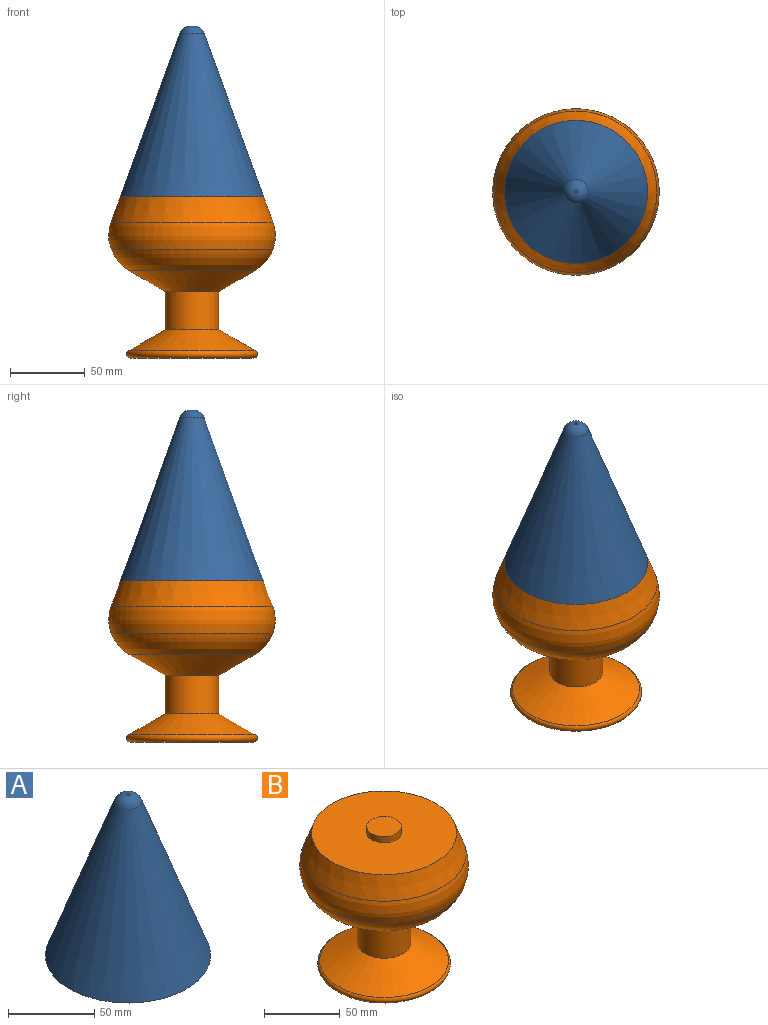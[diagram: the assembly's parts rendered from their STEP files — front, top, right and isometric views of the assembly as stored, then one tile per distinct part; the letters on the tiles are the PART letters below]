
ASSEMBLY  parts=2 mates=1
PART A: 6 faces, bbox 95.9x95.9x114.3 mm
  f0: plane 1.99x1.99mm, normal (0,0,1), area 3.1mm2, adj f1
  f1: torus R=0.99mm, axis (0,0,1), area 298.2mm2, adj f0,f2
  f2: cone r=61.8mm half-angle=20deg, axis (0,0,-1), area 20491.8mm2, adj f1,f3
  f3: plane 95.86x95.86mm, normal (0,0,-1), area 6710.8mm2, adj f2,f4
  f4: cylinder r=12.7mm len=25.4mm, axis (0,0,-1), area 506.7mm2, adj f3,f5
  f5: plane 25.4x25.4mm, normal (0,0,-1), area 506.7mm2, adj f4
PART B: 12 faces, bbox 120.7x120.7x113 mm
  f0: cone r=61.8mm half-angle=20deg, axis (0,0,-1), area 5816mm2, adj f7,f8
  f1: cone r=50.8mm half-angle=60deg, axis (0,0,-1), area 5430.4mm2, adj f3,f11
  f2: plane 82.64x82.64mm, normal (0,0,-1), area 5363.9mm2, adj f11
  f3: cylinder r=17.8mm len=35.61mm, axis (0,0,-1), area 2841.5mm2, adj f1,f4
  f4: cone r=17.8mm half-angle=60deg, axis (0,0,1), area 5369.6mm2, adj f3,f6
  f5: cone r=57.45mm half-angle=20deg, axis (0,0,1), area 14.7mm2, adj f6,f7
  f6: torus R=29.06mm, axis (0,0,1), area 5741.3mm2, adj f4,f5
  f7: torus R=29.07mm, axis (0,0,-1), area 6458.3mm2, adj f0,f5
  f8: plane 95.86x95.86mm, normal (0,0,1), area 6807.1mm2, adj f0,f9
  f9: cylinder r=11.43mm len=22.86mm, axis (0,0,-1), area 364.8mm2, adj f8,f10
  f10: plane 22.86x22.86mm, normal (0,0,1), area 410.4mm2, adj f9
  f11: torus R=41.32mm, axis (0,0,1), area 1802.1mm2, adj f1,f2
PLACE A t=(-9.29,-0.77,17.1)mm
PLACE B t=(-9.29,-0.77,17.1)mm
MATE fastened A.f1 <-> B.f0  axis (0,0,-1) through (-9.29,-0.77,125.05)mm
